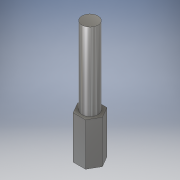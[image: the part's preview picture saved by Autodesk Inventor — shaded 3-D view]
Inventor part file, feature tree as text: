
AUTODESK INVENTOR PART (.ipt)
format: ipt  version: 2017 SP1 (Build 210196100, 196)  size: 114,688 bytes
history: native  units: in
note: dims shown in document units (in); Inventor stores cm internally (conversion verified against a paired STEP export)
features: extrude x3, sketch x3
ambient origin geometry x8: Origin, YZ Plane, XZ Plane, XY Plane, X Axis, Y Axis, Z Axis, Center Point
bodies: Solid1 (feature_tree)
feature tree (6):
  extrude  "Extrusion1"  Depth=1.0in TaperAngle=0.0deg
  extrude  "Extrusion2"  Depth=1.8125in TaperAngle=0.0deg
  extrude  "Extrusion3"  Depth=1.0in TaperAngle=0.0deg
  sketch  "Sketch1"  dims[d0=0.5in d1=1.0in d2=0.0in]
  sketch  "Sketch2"  dims[d3=0.375in d4=1.8125in d5=0.0in]
  sketch  "Sketch3"  dims[d7=0.15in d8=1.0in d9=0.0in]
